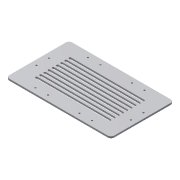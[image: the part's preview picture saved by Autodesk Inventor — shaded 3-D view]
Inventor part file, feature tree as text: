
AUTODESK INVENTOR PART (.ipt)
format: ipt  version: 2014 (Build 180170000, 170)  size: 224,768 bytes
history: native  units: mm
features: extrude x4, sketch x4, fillet x1
ambient origin geometry x8: Origin, YZ Plane, XZ Plane, XY Plane, X Axis, Y Axis, Z Axis, Center Point
bodies: Solid1 (feature_tree)
feature tree (9):
  extrude  "Extrusion1"  Depth=100.0mm
  extrude  "Extrusion2"  Depth=45.0mm
  extrude  "Extrusion3"  Depth=30.0mm
  fillet  "Fillet1"  Radius=30.0mm
  extrude  "Extrusion4"  Depth=4.0mm
  sketch  "Sketch1"  dims[d0=200.0mm d1=100.0mm]
  sketch  "Sketch2"  dims[d2=4.0mm d3=0.0mm d6=45.0mm]
  sketch  "Sketch3"  dims[d8=30.0mm d9=30.0mm d11=30.0mm]
  sketch  "Sketch4"  dims[d13=25.0mm d14=7.5mm d15=7.5mm d16=50.0mm d17=10.0mm d18=12.5mm d19=4.0mm d20=12.5mm d21=12.5mm d22=4.0mm d23=0.0mm d24=12.5mm d25=4.0mm d26=0.0mm d27=8.0mm d28=90.0mm d30=10.0mm d31=10.0mm d33=10.0mm d35=175.0mm d36=2.5mm d37=87.5mm d38=4.0mm d39=0.0mm]
